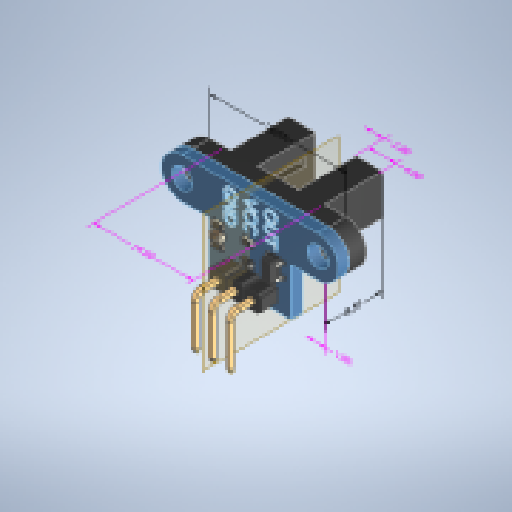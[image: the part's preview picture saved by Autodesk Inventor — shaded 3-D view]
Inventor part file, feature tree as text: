
AUTODESK INVENTOR PART (.ipt)
format: ipt  version: 2024 (Build 280153000, 153)  size: 778,240 bytes
history: native  units: mm
features: other x28, extrude x2, sketch x2, move_body x2, direct_edit x1, projected_geometry x1
ambient origin geometry x8: Origin, YZ Plane, XZ Plane, XY Plane, X Axis, Y Axis, Z Axis, Center Point
bodies: Solid1 (feature_tree), Solid2 (feature_tree), Solid3 (feature_tree), Solid4 (feature_tree), Solid5 (feature_tree), Solid6 (feature_tree), Solid7 (feature_tree), Solid8 (feature_tree), Solid9 (feature_tree), Solid10 (feature_tree), Solid11 (feature_tree), Solid12 (feature_tree), Solid13 (feature_tree), Solid14 (feature_tree)
feature tree (36):
  other  "Annotations"
  other  "Motor Encoder Diodes v1_1:1"
  other  "midplane for sensor"
  extrude  "Extrusion1"  Depth=6.0mm
  direct_edit  "Direct Edit2"
  extrude  "Extrusion2"  Depth=0.5mm TaperAngle=0.0deg
  other  "GND"
  other  "VCC"
  other  "DOUT"
  sketch  "Sketch1"  dims[d29=13.0mm d30=6.0mm]
  projected_geometry  "Projected Loop1"
  sketch  "Sketch2"  dims[d32=0.0mm d33=0.0mm d34=0.0mm d35=0.0mm d36=0.5mm d37=0.0mm d38=0.0mm d39=0.5mm d43=4.0mm d44=0.2mm d45=0.0mm d0=20.0mm d1=5.161813mm d13=7.394309mm d14=7.318151mm d15=4.0mm d2=3.743057mm d21=-3.790512mm d22=6.907149mm d23=2.8mm d24=6.604869mm d25=2.8mm d3=14.6mm d4=3.2mm d40=0.0mm d41=10.0mm d42=8.5mm d5=1.871037mm d6=2.2mm d7=5.116389mm d8=4.633405mm d9=5.6mm]
  other  "SOLID_1:1"
  other  "SOLID (1)_1:1"
  other  "SOLID (1)_1:2"
  other  "SOLID (1)_1:3"
  other  "SOLID (3)_1:1"
  other  "SOLID (4)_1:1"
  other  "COMPOUND_1:1"
  other  "DS1022-1x7RUF11 v2_1:1"
  other  "DS1022-1x7RUF11 v2_1:2"
  other  "DS1022-1x7RUF11 v2_1:3"
  other  "DS1022-1x7RUF11 v2_1:4"
  other  "DS1022-1x7RUF11 v2_1:5"
  other  "DS1022-1x7RUF11 v2_1:6"
  move_body  "Move2"
  move_body  "Move3"
  other  "Linear Dimension 1"
  other  "Linear Dimension 2"
  other  "Linear Dimension 3"
  other  "Linear Dimension 4"
  other  "Linear Dimension 5"
  other  "Linear Dimension 6"
  other  "Linear Dimension 9"
  other  "Linear Dimension 10"
  other  "Linear Dimension 12"
